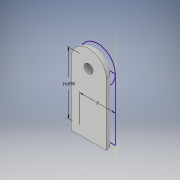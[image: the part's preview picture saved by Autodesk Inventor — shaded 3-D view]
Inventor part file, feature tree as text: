
AUTODESK INVENTOR PART (.ipt)
format: ipt  version: 2019 (Build 230136000, 136)  size: 117,760 bytes
history: native  units: mm
features: other x1, sketch x1, extrude x1, hole x1, fillet x1
ambient origin geometry x8: Origin, YZ Plane, XZ Plane, XY Plane, X Axis, Y Axis, Z Axis, Center Point
bodies: Body1 (feature_tree)
feature tree (5):
  other  "Bryła1"
  sketch  "Szkic1"
  extrude  "Wyciągnięcie proste1"  Depth=8.0mm
  hole  "Otwór1"  [1 undecoded]
  fillet  "Zaokrąglenie1"  Radius=2.0mm
note: 1 required parameter value undecoded (feature->parameter linkage not recoverable at this tier; creation-order binding heuristic only, values carry confidence <= 0.55)
